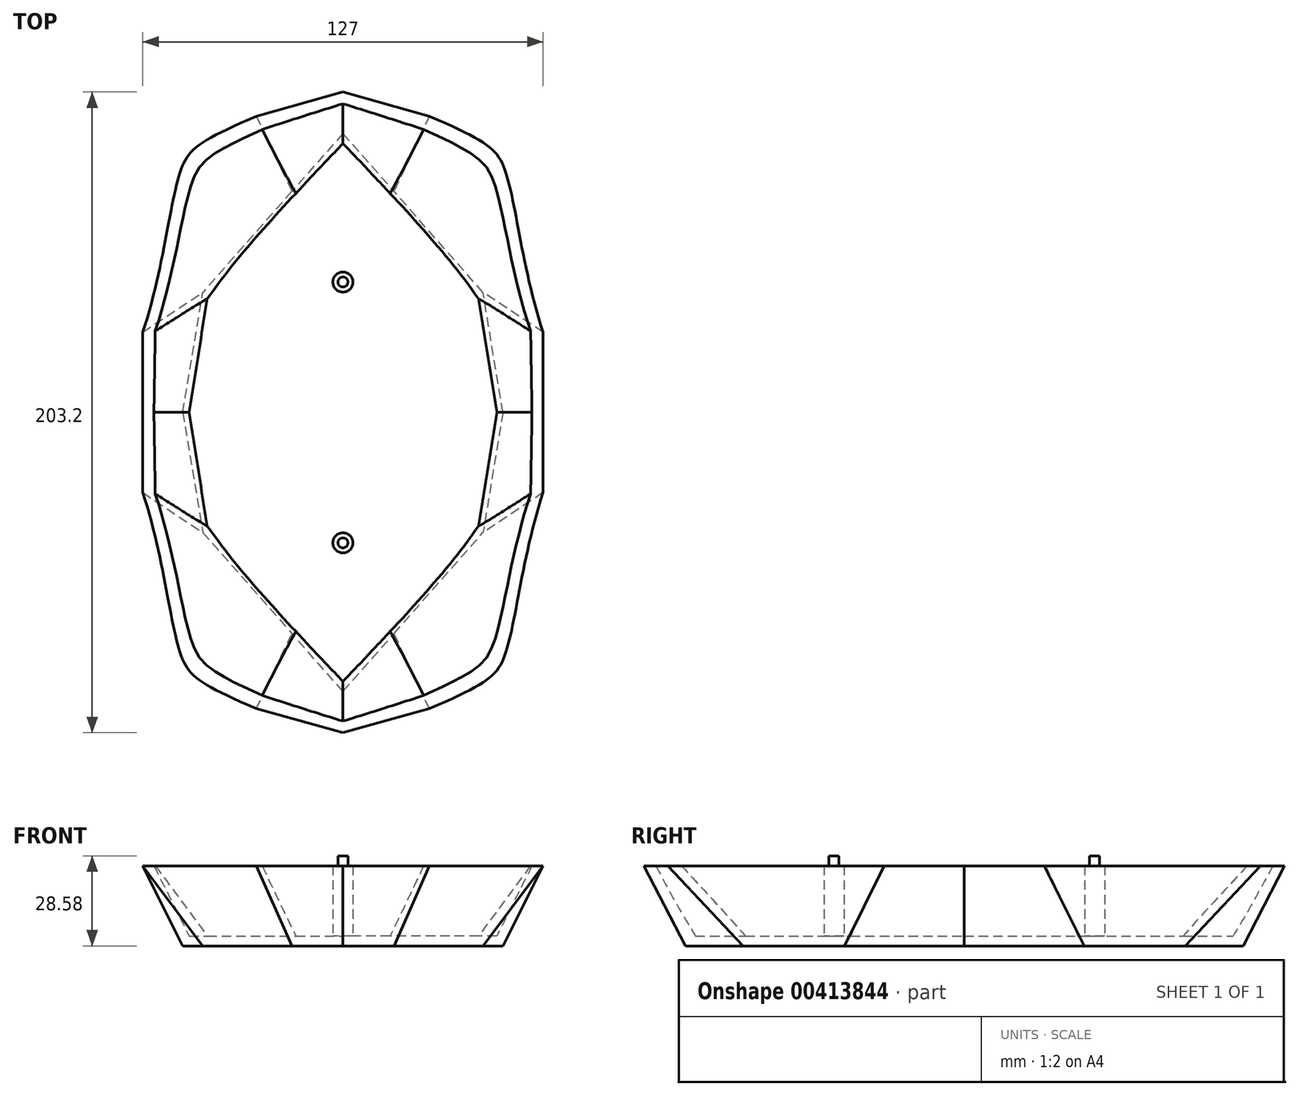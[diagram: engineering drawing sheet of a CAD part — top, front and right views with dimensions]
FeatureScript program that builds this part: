
annotation { "Feature Type Name" : "Feature", "Feature Type Description" : "" }
export const myFeature = defineFeature(function(context is Context, id is Id, definition is map)
    precondition{}
    {
        {
            var Q0;
            Q0=qCreatedBy(makeId("Top.planeOp"),FACE);
            var sketch = newSketch(context, id + "F0", { "sketchPlane" : qUnion([Q0])});
            skLineSegment(sketch, "E0", {"start": v(-63.5, 0) * mm, "end": v(-63.5, -25.4) * mm});
            skLineSegment(sketch, "E1", {"start": v(0, -101.6) * mm, "end": v(-27.43, -93.95) * mm});
            skFitSpline(sketch, "E2", {"points": [v(-63.5, -25.4) * mm, v(-51.66, -76.12) * mm, v(-27.43, -93.95) * mm], "startDerivative": vector(34.98, -106.28) * mm, "endDerivative": vector(126.69, -55.22) * mm});
            skFitSpline(sketch, "E3.MirrorCS", {"points": [v(-63.5, 25.4) * mm, v(-51.66, 76.12) * mm, v(-27.43, 93.95) * mm], "startDerivative": vector(34.98, 106.28) * mm, "endDerivative": vector(126.69, 55.22) * mm});
            skLineSegment(sketch, "E4.MirrorCS", {"start": v(0, 101.6) * mm, "end": v(-27.43, 93.95) * mm});
            skLineSegment(sketch, "E5.MirrorCS", {"start": v(-63.5, 0) * mm, "end": v(-63.5, 25.4) * mm});
            skLineSegment(sketch, "E6.MirrorCS", {"start": v(0, -101.6) * mm, "end": v(27.43, -93.95) * mm});
            skFitSpline(sketch, "E7.MirrorCS", {"points": [v(63.5, 25.4) * mm, v(51.66, 76.12) * mm, v(27.43, 93.95) * mm], "startDerivative": vector(-34.98, 106.28) * mm, "endDerivative": vector(-126.69, 55.22) * mm});
            skLineSegment(sketch, "E8.MirrorCS", {"start": v(63.5, 0) * mm, "end": v(63.5, -25.4) * mm});
            skFitSpline(sketch, "E9.MirrorCS", {"points": [v(63.5, -25.4) * mm, v(51.66, -76.12) * mm, v(27.43, -93.95) * mm], "startDerivative": vector(-34.98, -106.28) * mm, "endDerivative": vector(-126.69, -55.22) * mm});
            skLineSegment(sketch, "E10.MirrorCS", {"start": v(0, 101.6) * mm, "end": v(27.43, 93.95) * mm});
            skLineSegment(sketch, "E11.MirrorCS", {"start": v(63.5, 0) * mm, "end": v(63.5, 25.4) * mm});
            skLineSegment(sketch, "E12", {"start": v(63.5, 0) * mm, "end": v(-63.5, 0) * mm});
            skLineSegment(sketch, "E13", {"start": v(0, 101.6) * mm, "end": v(0, -101.6) * mm});
            skSolve(sketch);
        }
        {
            var Q0;
            Q0=qCreatedBy(makeId("Top.planeOp"),FACE);
            cPlane(context, id + "F1", {"entities" : qUnion([Q0]), "cplaneType" : CPlaneType.OFFSET, "offset" : 25.4 * mm, "oppositeDirection" : true, "width" : 152.4 * mm, "height" : 152.4 * mm});
        }
        {
            var Q0;
            Q0=qCreatedBy(id+"F1.planeOp",FACE);
            var sketch = newSketch(context, id + "F2", { "sketchPlane" : qUnion([Q0])});
            skLineSegment(sketch, "E14", {"start": v(-50.8, 0) * mm, "end": v(-44.45, -38.06) * mm});
            skLineSegment(sketch, "E15", {"start": v(0, -88.46) * mm, "end": v(-16.18, -70.12) * mm});
            skLineSegment(sketch, "E16.MirrorCS", {"start": v(0, 88.46) * mm, "end": v(-16.18, 70.12) * mm});
            skLineSegment(sketch, "E17.MirrorCS", {"start": v(-50.8, 0) * mm, "end": v(-44.45, 38.06) * mm});
            skLineSegment(sketch, "E18.MirrorCS", {"start": v(50.8, 0) * mm, "end": v(44.45, 38.06) * mm});
            skLineSegment(sketch, "E19.MirrorCS", {"start": v(0, 88.46) * mm, "end": v(16.18, 70.12) * mm});
            skLineSegment(sketch, "E20.MirrorCS", {"start": v(0, -88.46) * mm, "end": v(16.18, -70.12) * mm});
            skLineSegment(sketch, "E21.MirrorCS", {"start": v(50.8, 0) * mm, "end": v(44.45, -38.06) * mm});
            skLineSegment(sketch, "E22", {"start": v(-33.3, -50.71) * mm, "end": v(-16.18, -70.12) * mm});
            skLineSegment(sketch, "E23.trimOffspring", {"start": v(-33.3, -50.71) * mm, "end": v(-44.45, -38.06) * mm});
            skLineSegment(sketch, "E24.MirrorCS", {"start": v(-33.3, 50.71) * mm, "end": v(-16.18, 70.12) * mm});
            skLineSegment(sketch, "E25.MirrorCS", {"start": v(33.3, -50.71) * mm, "end": v(16.18, -70.12) * mm});
            skLineSegment(sketch, "E26.trimOffspring", {"start": v(-33.3, 50.71) * mm, "end": v(-44.45, 38.06) * mm});
            skLineSegment(sketch, "E27.trimOffspring", {"start": v(33.3, -50.71) * mm, "end": v(44.45, -38.06) * mm});
            skLineSegment(sketch, "E28.MirrorCS", {"start": v(33.3, 50.71) * mm, "end": v(16.18, 70.12) * mm});
            skLineSegment(sketch, "E29.trimOffspring", {"start": v(33.3, 50.71) * mm, "end": v(44.45, 38.06) * mm});
            skLineSegment(sketch, "E30", {"start": v(50.8, 0) * mm, "end": v(-50.8, 0) * mm});
            skLineSegment(sketch, "E31", {"start": v(0, 88.46) * mm, "end": v(0, -88.46) * mm});
            skSolve(sketch);
        }
        {
            var Q0;
            Q0=makeQuery(id+"F0.imprint","IMPRINT",FACE,{"disambiguationData":[TD([[makeQuery(id+"F0.imprint","IMPRINT",EDGE,{"derivedFrom":sQuery(id+"F0.wireOp",EDGE,"E3.MirrorCS")}),-1.0]])]});
            var Q1;
            {var subQ1=sQuery(id+"F2.wireOp",EDGE,"E16.MirrorCS");Q1=makeQuery(id+"F2.imprint","IMPRINT",FACE,{"disambiguationData":[TD([[makeQuery(id+"F2.imprint","IMPRINT",EDGE,{"derivedFrom":subQ1}),1.0]])]});}
            loft(context, id + "F3", {"sheetProfilesArray" : [{ "sheetProfileEntities" : qUnion([Q0]) }, { "sheetProfileEntities" : qUnion([Q1]) }]});
        }
        {
            var Q1;
            {var subQ1=sQuery(id+"F0.wireOp",EDGE,"E0");Q1=makeQuery(id+"F0.imprint","IMPRINT",FACE,{"disambiguationData":[TD([[makeQuery(id+"F0.imprint","IMPRINT",EDGE,{"derivedFrom":subQ1}),1.0]])]});}
            var Q2;
            {var subQ4=sQuery(id+"F2.wireOp",EDGE,"E14");Q2=makeQuery(id+"F2.imprint","IMPRINT",FACE,{"disambiguationData":[TD([[makeQuery(id+"F2.imprint","IMPRINT",EDGE,{"derivedFrom":subQ4}),1.0]])]});}
            var Q3;
            Q3=sQuery(id+"F0.wireOp",VERTEX,"E1.start");
            var Q4;
            Q4=sQuery(id+"F2.wireOp",VERTEX,"E31.end");
            loft(context, id + "F4", {"operationType" : NewBodyOperationType.ADD, "sheetProfilesArray" : [{ "sheetProfileEntities" : qUnion([Q1]) }, { "sheetProfileEntities" : qUnion([Q2]) }], "matchConnections" : true, "connections" : [{ "connectionEntities" : qUnion([Q3, Q4]), "connectionEdgeQueries" : qUnion([]), "connectionEdgeParameters" : [] }]});
        }
        {
            var Q1;
            {var subQ4=sQuery(id+"F0.wireOp",EDGE,"E6.MirrorCS");Q1=makeQuery(id+"F0.imprint","IMPRINT",FACE,{"disambiguationData":[TD([[makeQuery(id+"F0.imprint","IMPRINT",EDGE,{"derivedFrom":subQ4}),1.0]])]});}
            var Q2;
            {var subQ1=sQuery(id+"F2.wireOp",EDGE,"E20.MirrorCS");Q2=makeQuery(id+"F2.imprint","IMPRINT",FACE,{"disambiguationData":[TD([[makeQuery(id+"F2.imprint","IMPRINT",EDGE,{"derivedFrom":subQ1}),1.0]])]});}
            var Q3;
            Q3=sQuery(id+"F2.wireOp",VERTEX,"E18.MirrorCS.start");
            var Q4;
            Q4=sQuery(id+"F0.wireOp",VERTEX,"E11.MirrorCS.start");
            loft(context, id + "F5", {"operationType" : NewBodyOperationType.ADD, "sheetProfilesArray" : [{ "sheetProfileEntities" : qUnion([Q1]) }, { "sheetProfileEntities" : qUnion([Q2]) }], "matchConnections" : true, "connections" : [{ "connectionEntities" : qUnion([Q3, Q4]), "connectionEdgeQueries" : qUnion([]), "connectionEdgeParameters" : [] }]});
        }
        {
            var Q1;
            Q1=makeQuery(id+"F0.imprint","IMPRINT",FACE,{"disambiguationData":[TD([[makeQuery(id+"F0.imprint","IMPRINT",EDGE,{"derivedFrom":sQuery(id+"F0.wireOp",EDGE,"E7.MirrorCS")}),1.0]])]});
            var Q2;
            {var subQ0=sQuery(id+"F2.wireOp",EDGE,"E18.MirrorCS");Q2=makeQuery(id+"F2.imprint","IMPRINT",FACE,{"disambiguationData":[TD([[makeQuery(id+"F2.imprint","IMPRINT",EDGE,{"derivedFrom":subQ0}),1.0]])]});}
            loft(context, id + "F6", {"operationType" : NewBodyOperationType.ADD, "sheetProfilesArray" : [{ "sheetProfileEntities" : qUnion([Q1]) }, { "sheetProfileEntities" : qUnion([Q2]) }]});
        }
        {
            var Q0;
            {var subQ9=sQuery(id+"F0.wireOp",EDGE,"E6.MirrorCS");var subQ13=sQuery(id+"F0.wireOp",EDGE,"E0");Q0=makeQuery(id+"F6.boolean.opBoolean","MERGE",FACE,{"derivedFrom":[makeQuery(id+"F5.boolean.opBoolean","MERGE",FACE,{"derivedFrom":[makeQuery(id+"F4.boolean.opBoolean","MERGE",FACE,{"derivedFrom":[makeQuery(id+"F3.opLoft","CAP_FACE",FACE,{"disambiguationData":[OSD([makeQuery(id+"F0.imprint","IMPRINT",FACE,{"disambiguationData":[TD([[makeQuery(id+"F0.imprint","IMPRINT",EDGE,{"derivedFrom":sQuery(id+"F0.wireOp",EDGE,"E3.MirrorCS")}),-1.0]])]})])],"isStart":true}),makeQuery(id+"F4.opLoft","CAP_FACE",FACE,{"disambiguationData":[OSD([makeQuery(id+"F0.imprint","IMPRINT",FACE,{"disambiguationData":[TD([[makeQuery(id+"F0.imprint","IMPRINT",EDGE,{"derivedFrom":subQ13}),1.0]])]})])],"isStart":true})]}),makeQuery(id+"F5.opLoft","CAP_FACE",FACE,{"disambiguationData":[OSD([makeQuery(id+"F0.imprint","IMPRINT",FACE,{"disambiguationData":[TD([[makeQuery(id+"F0.imprint","IMPRINT",EDGE,{"derivedFrom":subQ9}),1.0]])]})])],"isStart":true})]}),makeQuery(id+"F6.opLoft","CAP_FACE",FACE,{"disambiguationData":[OSD([makeQuery(id+"F0.imprint","IMPRINT",FACE,{"disambiguationData":[TD([[makeQuery(id+"F0.imprint","IMPRINT",EDGE,{"derivedFrom":sQuery(id+"F0.wireOp",EDGE,"E7.MirrorCS")}),1.0]])]})])],"isStart":true})]});}
            shell(context, id + "F7", {"entities" : qUnion([Q0]), "thickness" : 3.17 * mm});
        }
        {
            var Q0;
            Q0=qCreatedBy(id+"F1.planeOp",FACE);
            var sketch = newSketch(context, id + "F8", { "sketchPlane" : qUnion([Q0])});
            skCircle(sketch, "E32", {"center": v(0, 41.36) * mm, "radius": 3.18 * mm});
            skLineSegment(sketch, "E33", {"start": v(0, 0) * mm, "end": v(19.64, 0) * mm});
            skCircle(sketch, "E34.MirrorC", {"center": v(0, -41.36) * mm, "radius": 3.18 * mm});
            skSolve(sketch);
        }
        {
            var Q0;
            Q0 = qSketchRegion(id + "F8", true);
            extrude(context, id + "F9", {"entities" : qUnion([Q0]), "operationType" : NewBodyOperationType.ADD, "depth" : 25.4 * mm});
        }
        {
            var Q0;
            Q0=makeQuery(id+"F9.opExtrude","CAP_FACE",FACE,{"disambiguationData":[OSD([sQuery(id+"F8.wireOp",EDGE,"E34.MirrorC")])],"isStart":false});
            var sketch = newSketch(context, id + "F10", { "sketchPlane" : qUnion([Q0])});
            skCircle(sketch, "E35", {"center": v(0, -41.36) * mm, "radius": 1.59 * mm});
            skLineSegment(sketch, "E36", {"start": v(0, 0) * mm, "end": v(-8.73, 0) * mm});
            skCircle(sketch, "E37.MirrorC", {"center": v(0, 41.36) * mm, "radius": 1.59 * mm});
            skSolve(sketch);
        }
        {
            var Q0;
            Q0 = qSketchRegion(id + "F10", true);
            extrude(context, id + "F11", {"entities" : qUnion([Q0]), "operationType" : NewBodyOperationType.ADD, "depth" : 3.17 * mm});
        }
    });
